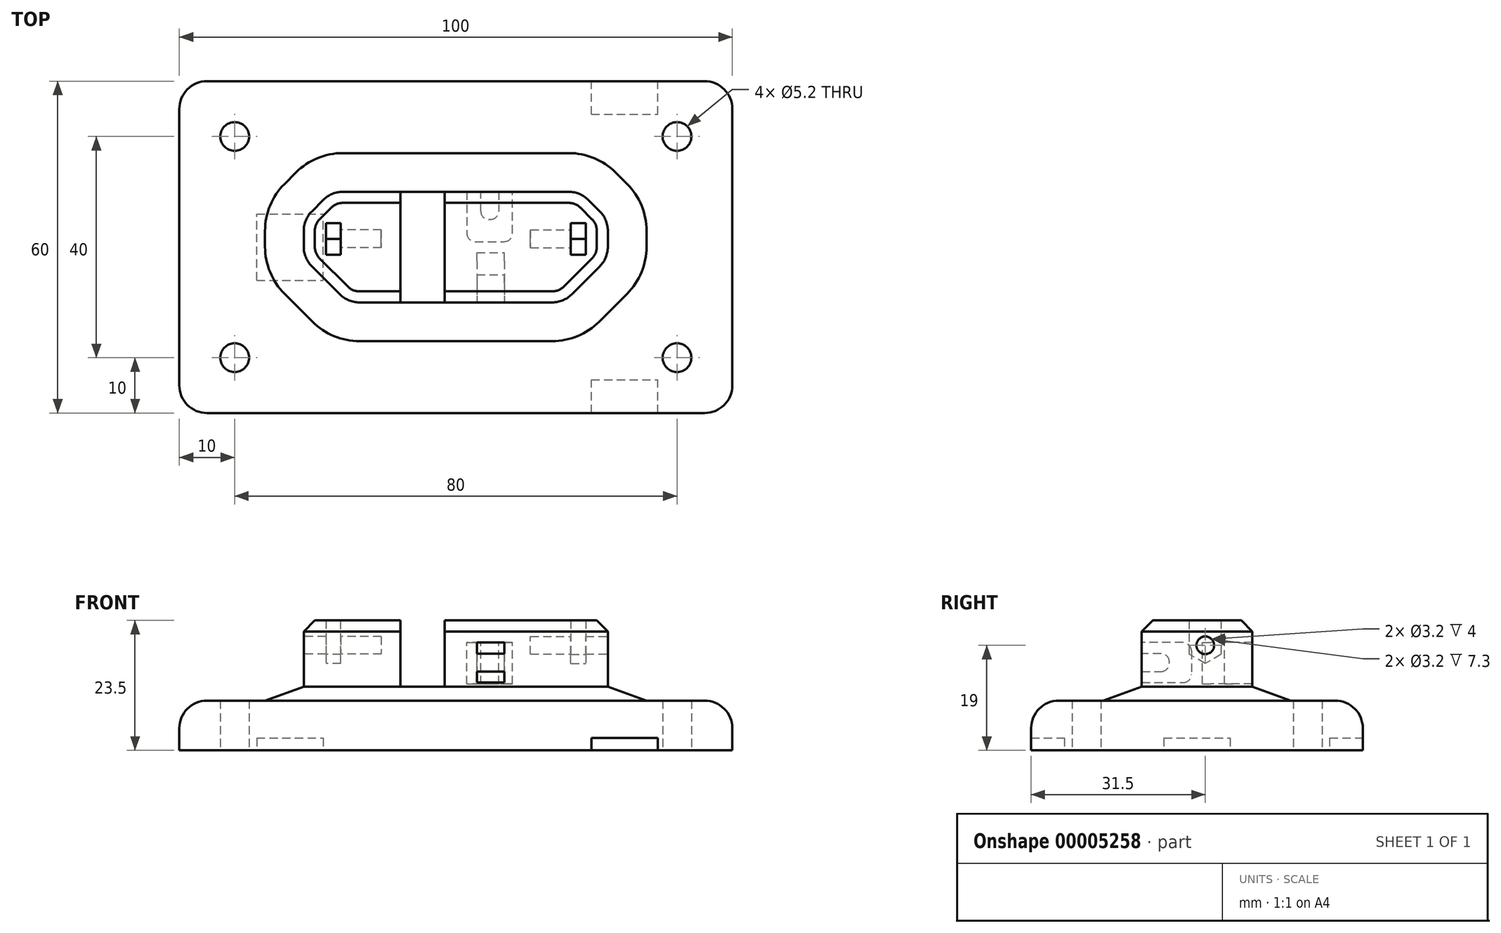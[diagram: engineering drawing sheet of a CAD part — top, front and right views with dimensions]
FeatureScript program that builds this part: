
annotation { "Feature Type Name" : "Feature", "Feature Type Description" : "" }
export const myFeature = defineFeature(function(context is Context, id is Id, definition is map)
    precondition{}
    {
        {
            var Q0;
            Q0=qCreatedBy(makeId("Top.planeOp"),FACE);
            var sketch = newSketch(context, id + "F0", { "sketchPlane" : qUnion([Q0])});
            skLineSegment(sketch, "E0.rect.bottom", {"start": v(-45, 30) * mm, "end": v(45, 30) * mm});
            skLineSegment(sketch, "E0.rect.top", {"start": v(-45, -30) * mm, "end": v(45, -30) * mm});
            skLineSegment(sketch, "E0.rect.left", {"start": v(-50, 25) * mm, "end": v(-50, -25) * mm});
            skLineSegment(sketch, "E0.rect.right", {"start": v(50, 25) * mm, "end": v(50, -25) * mm});
            skPoint(sketch, "E0.rect.middle", {"position": v(0, 0) * mm});
            skCircle(sketch, "E1", {"center": v(-40, 20) * mm, "radius": 2.6 * mm});
            skCircle(sketch, "E2", {"center": v(40, 20) * mm, "radius": 2.6 * mm});
            skCircle(sketch, "E3", {"center": v(40, -20) * mm, "radius": 2.6 * mm});
            skCircle(sketch, "E4", {"center": v(-40, -20) * mm, "radius": 2.6 * mm});
            skPoint(sketch, "E5.visualSharp", {"position": v(-50, 30) * mm});
            skArc(sketch, "E5.filletArc", {"start": v(-45, 30) * mm, "mid": v(-48.54, 28.54) * mm, "end": v(-50, 25) * mm});
            skPoint(sketch, "E6.visualSharp", {"position": v(50, 30) * mm});
            skArc(sketch, "E6.filletArc", {"start": v(50, 25) * mm, "mid": v(48.54, 28.54) * mm, "end": v(45, 30) * mm});
            skPoint(sketch, "E7.visualSharp", {"position": v(50, -30) * mm});
            skArc(sketch, "E7.filletArc", {"start": v(45, -30) * mm, "mid": v(48.54, -28.54) * mm, "end": v(50, -25) * mm});
            skPoint(sketch, "E8.visualSharp", {"position": v(-50, -30) * mm});
            skArc(sketch, "E8.filletArc", {"start": v(-50, -25) * mm, "mid": v(-48.54, -28.54) * mm, "end": v(-45, -30) * mm});
            skSolve(sketch);
        }
        {
            var Q0;
            Q0=qSketchRegion(id+"F0",true);
            extrude(context, id + "F1", {"entities" : qUnion([Q0]), "depth" : 9 * mm});
        }
        {
            var Q0;
            Q0=makeQuery(id+"F1.opExtrude","CAP_FACE",FACE,{"disambiguationData":[OSD([sQuery(id+"F0.wireOp",EDGE,"E0.rect.bottom"),sQuery(id+"F0.wireOp",EDGE,"E0.rect.top"),sQuery(id+"F0.wireOp",EDGE,"E0.rect.left"),sQuery(id+"F0.wireOp",EDGE,"E0.rect.right"),sQuery(id+"F0.wireOp",EDGE,"E1"),sQuery(id+"F0.wireOp",EDGE,"E2"),sQuery(id+"F0.wireOp",EDGE,"E3"),sQuery(id+"F0.wireOp",EDGE,"E4"),sQuery(id+"F0.wireOp",EDGE,"E5.filletArc"),sQuery(id+"F0.wireOp",EDGE,"E6.filletArc"),sQuery(id+"F0.wireOp",EDGE,"E7.filletArc"),sQuery(id+"F0.wireOp",EDGE,"E8.filletArc")])],"isStart":true});
            var sketch = newSketch(context, id + "F2", { "sketchPlane" : qUnion([Q0])});
            skLineSegment(sketch, "E9.rect.bottom", {"start": v(-36, 6) * mm, "end": v(-24, 6) * mm});
            skLineSegment(sketch, "E9.rect.top", {"start": v(-36, -6) * mm, "end": v(-24, -6) * mm});
            skLineSegment(sketch, "E9.rect.left", {"start": v(-36, 6) * mm, "end": v(-36, -6) * mm});
            skLineSegment(sketch, "E9.rect.right", {"start": v(-24, 6) * mm, "end": v(-24, -6) * mm});
            skPoint(sketch, "E9.rect.middle", {"position": v(-30, 0) * mm});
            skLineSegment(sketch, "E10.rect.bottom", {"start": v(24.52, 36) * mm, "end": v(36.52, 36) * mm});
            skLineSegment(sketch, "E10.rect.top", {"start": v(24.52, 24) * mm, "end": v(36.52, 24) * mm});
            skLineSegment(sketch, "E10.rect.left", {"start": v(24.52, 36) * mm, "end": v(24.52, 24) * mm});
            skLineSegment(sketch, "E10.rect.right", {"start": v(36.52, 36) * mm, "end": v(36.52, 24) * mm});
            skPoint(sketch, "E10.rect.middle", {"position": v(30.52, 30) * mm});
            skLineSegment(sketch, "E11.rect.bottom", {"start": v(24.52, -24) * mm, "end": v(36.52, -24) * mm});
            skLineSegment(sketch, "E11.rect.top", {"start": v(24.52, -36) * mm, "end": v(36.52, -36) * mm});
            skLineSegment(sketch, "E11.rect.left", {"start": v(24.52, -24) * mm, "end": v(24.52, -36) * mm});
            skLineSegment(sketch, "E11.rect.right", {"start": v(36.52, -24) * mm, "end": v(36.52, -36) * mm});
            skPoint(sketch, "E11.rect.middle", {"position": v(30.52, -30) * mm});
            skLineSegment(sketch, "E12", {"start": v(0, 0) * mm, "end": v(50, 0) * mm});
            skSolve(sketch);
        }
        {
            var Q0;
            Q0=qSketchRegion(id+"F2",true);
            extrude(context, id + "F3", {"entities" : qUnion([Q0]), "operationType" : NewBodyOperationType.REMOVE, "oppositeDirection" : true, "depth" : 2.25 * mm});
        }
        {
            var Q0;
            Q0=makeQuery(id+"F1.opExtrude","CAP_FACE",FACE,{"disambiguationData":[OSD([sQuery(id+"F0.wireOp",EDGE,"E0.rect.bottom"),sQuery(id+"F0.wireOp",EDGE,"E0.rect.top"),sQuery(id+"F0.wireOp",EDGE,"E0.rect.left"),sQuery(id+"F0.wireOp",EDGE,"E0.rect.right"),sQuery(id+"F0.wireOp",EDGE,"E1"),sQuery(id+"F0.wireOp",EDGE,"E2"),sQuery(id+"F0.wireOp",EDGE,"E3"),sQuery(id+"F0.wireOp",EDGE,"E4"),sQuery(id+"F0.wireOp",EDGE,"E5.filletArc"),sQuery(id+"F0.wireOp",EDGE,"E6.filletArc"),sQuery(id+"F0.wireOp",EDGE,"E7.filletArc"),sQuery(id+"F0.wireOp",EDGE,"E8.filletArc")])],"isStart":false});
            var sketch = newSketch(context, id + "F4", { "sketchPlane" : qUnion([Q0])});
            skPoint(sketch, "E13.orphan", {"position": v(-50, 0) * mm});
            skPoint(sketch, "E14.end.orphan", {"position": v(50, 0) * mm});
            skLineSegment(sketch, "E15.rect.bottom", {"start": v(-27.5, 10) * mm, "end": v(27.5, 10) * mm});
            skLineSegment(sketch, "E15.rect.top", {"start": v(-27.5, -10) * mm, "end": v(27.5, -10) * mm});
            skLineSegment(sketch, "E15.rect.left", {"start": v(-27.5, 10) * mm, "end": v(-27.5, -10) * mm});
            skLineSegment(sketch, "E15.rect.right", {"start": v(27.5, 10) * mm, "end": v(27.5, -10) * mm});
            skPoint(sketch, "E15.rect.middle", {"position": v(0, 0) * mm});
            skSolve(sketch);
        }
        {
            var Q0;
            Q0=qSketchRegion(id+"F4",true);
            extrude(context, id + "F5", {"entities" : qUnion([Q0]), "operationType" : NewBodyOperationType.ADD, "depth" : 14.5 * mm});
        }
        {
            var Q0;
            Q0=makeQuery(id+"F5.opExtrude","SWEPT_EDGE",EDGE,{"disambiguationData":[OSD([sQuery(id+"F4.wireOp",EDGE,"E15.rect.top"),sQuery(id+"F4.wireOp",EDGE,"E15.rect.left")])]});
            var Q1;
            Q1=makeQuery(id+"F5.opExtrude","SWEPT_EDGE",EDGE,{"disambiguationData":[OSD([sQuery(id+"F4.wireOp",EDGE,"E15.rect.top"),sQuery(id+"F4.wireOp",EDGE,"E15.rect.right")])]});
            chamfer(context, id + "F6", {"entities" : qUnion([Q0, Q1]), "width" : 8 * mm, "tangentPropagation" : true});
        }
        {
            var Q0;
            Q0=makeQuery(id+"F5.opExtrude","SWEPT_EDGE",EDGE,{"disambiguationData":[OSD([sQuery(id+"F4.wireOp",EDGE,"E15.rect.bottom"),sQuery(id+"F4.wireOp",EDGE,"E15.rect.left")])]});
            var Q1;
            Q1=makeQuery(id+"F5.opExtrude","SWEPT_EDGE",EDGE,{"disambiguationData":[OSD([sQuery(id+"F4.wireOp",EDGE,"E15.rect.bottom"),sQuery(id+"F4.wireOp",EDGE,"E15.rect.right")])]});
            chamfer(context, id + "F7", {"entities" : qUnion([Q0, Q1]), "width" : 5 * mm, "tangentPropagation" : true});
        }
        {
            var Q0;
            Q0=makeQuery(id+"F5.opExtrude","CAP_FACE",FACE,{"disambiguationData":[OSD([sQuery(id+"F4.wireOp",EDGE,"E15.rect.bottom"),sQuery(id+"F4.wireOp",EDGE,"E15.rect.top"),sQuery(id+"F4.wireOp",EDGE,"E15.rect.left"),sQuery(id+"F4.wireOp",EDGE,"E15.rect.right")])],"isStart":false});
            var sketch = newSketch(context, id + "F8", { "sketchPlane" : qUnion([Q0])});
            skLineSegment(sketch, "E16.rect.bottom", {"start": v(-10, 10) * mm, "end": v(-2, 10) * mm});
            skLineSegment(sketch, "E16.rect.top", {"start": v(-10, -10) * mm, "end": v(-2, -10) * mm});
            skLineSegment(sketch, "E16.rect.left", {"start": v(-10, 10) * mm, "end": v(-10, -10) * mm});
            skLineSegment(sketch, "E16.rect.right", {"start": v(-2, 10) * mm, "end": v(-2, -10) * mm});
            skPoint(sketch, "E16.rect.middle", {"position": v(-6, 0) * mm});
            skSolve(sketch);
        }
        {
            var Q0;
            Q0=qSketchRegion(id+"F8",true);
            extrude(context, id + "F9", {"entities" : qUnion([Q0]), "operationType" : NewBodyOperationType.REMOVE, "oppositeDirection" : true, "depth" : 12 * mm});
        }
        {
            var Q0;
            {var subQ0=sQuery(id+"F4.wireOp",EDGE,"E15.rect.bottom");var subQ1=sQuery(id+"F4.wireOp",EDGE,"E15.rect.top");var subQ2=sQuery(id+"F4.wireOp",EDGE,"E15.rect.right");Q0=makeQuery(id+"F9.boolean.opBoolean","SPLIT",FACE,{"disambiguationData":[TD([makeQuery(id+"F5.opExtrude","SWEPT_FACE",FACE,{"disambiguationData":[OSD([subQ2])]})])],"derivedFrom":makeQuery(id+"F5.opExtrude","CAP_FACE",FACE,{"disambiguationData":[OSD([subQ0,subQ1,sQuery(id+"F4.wireOp",EDGE,"E15.rect.left"),subQ2])],"isStart":false})});}
            cPlane(context, id + "F10", {"entities" : qUnion([Q0]), "cplaneType" : CPlaneType.OFFSET, "offset" : 4 * mm, "oppositeDirection" : true, "width" : 150 * mm, "height" : 150 * mm});
        }
        {
            var Q0;
            Q0=makeQuery(id+"F5.opExtrude","SWEPT_FACE",FACE,{"disambiguationData":[OSD([sQuery(id+"F4.wireOp",EDGE,"E15.rect.left")])]});
            var sketch = newSketch(context, id + "F11", { "sketchPlane" : qUnion([Q0])});
            skCircle(sketch, "E17", {"center": v(-1.5, 19) * mm, "radius": 1.6 * mm});
            skSolve(sketch);
        }
        {
            var Q0;
            Q0=qSketchRegion(id+"F11",true);
            extrude(context, id + "F12", {"entities" : qUnion([Q0]), "operationType" : NewBodyOperationType.REMOVE, "oppositeDirection" : true, "depth" : 14 * mm});
        }
        {
            var Q0;
            Q0=makeQuery(id+"F5.opExtrude","SWEPT_FACE",FACE,{"disambiguationData":[OSD([sQuery(id+"F4.wireOp",EDGE,"E15.rect.right")])]});
            var sketch = newSketch(context, id + "F13", { "sketchPlane" : qUnion([Q0])});
            skCircle(sketch, "E18", {"center": v(1.5, 19) * mm, "radius": 1.6 * mm});
            skSolve(sketch);
        }
        {
            var Q0;
            Q0=qSketchRegion(id+"F13",true);
            extrude(context, id + "F14", {"entities" : qUnion([Q0]), "operationType" : NewBodyOperationType.REMOVE, "oppositeDirection" : true, "depth" : 14 * mm});
        }
        {
            var Q0;
            Q0=qCreatedBy(id+"F10.planeOp",FACE);
            var sketch = newSketch(context, id + "F15", { "sketchPlane" : qUnion([Q0])});
            skLineSegment(sketch, "E19", {"start": v(2, 10) * mm, "end": v(2, 1) * mm});
            skLineSegment(sketch, "E20", {"start": v(2, 1) * mm, "end": v(10.25, 1) * mm});
            skLineSegment(sketch, "E21", {"start": v(10.25, 1) * mm, "end": v(10.25, 10) * mm});
            skLineSegment(sketch, "E22", {"start": v(10.25, 10) * mm, "end": v(7.75, 10) * mm});
            skLineSegment(sketch, "E23", {"start": v(7.75, 10) * mm, "end": v(7.75, 5) * mm});
            skLineSegment(sketch, "E24", {"start": v(7.75, 5) * mm, "end": v(4.5, 5) * mm});
            skLineSegment(sketch, "E25", {"start": v(4.5, 5) * mm, "end": v(4.5, 10) * mm});
            skLineSegment(sketch, "E26", {"start": v(4.5, 10) * mm, "end": v(2, 10) * mm});
            skSolve(sketch);
        }
        {
            var Q0;
            Q0=qSketchRegion(id+"F15",true);
            extrude(context, id + "F16", {"entities" : qUnion([Q0]), "operationType" : NewBodyOperationType.REMOVE, "oppositeDirection" : true, "depth" : 7.5 * mm});
        }
        {
            var Q0;
            Q0=qCreatedBy(makeId("Right.planeOp"),FACE);
            cPlane(context, id + "F17", {"entities" : qUnion([Q0]), "cplaneType" : CPlaneType.OFFSET, "offset" : 8.8 * mm, "width" : 150 * mm, "height" : 150 * mm});
        }
        {
            var Q0;
            Q0=qCreatedBy(id+"F17.planeOp",FACE);
            var sketch = newSketch(context, id + "F18", { "sketchPlane" : qUnion([Q0])});
            skLineSegment(sketch, "E27", {"start": v(-10, 12.25) * mm, "end": v(-1, 12.25) * mm});
            skLineSegment(sketch, "E28", {"start": v(-1, 19.5) * mm, "end": v(-10, 19.5) * mm});
            skLineSegment(sketch, "E29", {"start": v(-10, 19.5) * mm, "end": v(-10, 17.5) * mm});
            skLineSegment(sketch, "E30", {"start": v(-1, 19.5) * mm, "end": v(-1, 12.25) * mm});
            skLineSegment(sketch, "E31", {"start": v(-10, 14.25) * mm, "end": v(-5, 14.25) * mm});
            skLineSegment(sketch, "E32", {"start": v(-5, 14.25) * mm, "end": v(-5, 17.5) * mm});
            skLineSegment(sketch, "E33", {"start": v(-5, 17.5) * mm, "end": v(-10, 17.5) * mm});
            skLineSegment(sketch, "E34.trimOffspring", {"start": v(-10, 14.25) * mm, "end": v(-10, 12.25) * mm});
            skSolve(sketch);
        }
        {
            var Q0;
            Q0 = qSketchRegion(id + "F18", true);
            extrude(context, id + "F19", {"entities" : qUnion([Q0]), "operationType" : NewBodyOperationType.REMOVE, "oppositeDirection" : true, "depth" : 5 * mm});
        }
        {
            var Q0;
            Q0=makeQuery(id+"F16.boolean.opBoolean","COPY",EDGE,{"derivedFrom":makeQuery(id+"F16.opExtrude","SWEPT_EDGE",EDGE,{"disambiguationData":[OSD([sQuery(id+"F15.wireOp",EDGE,"b27fa09f-654b-4976-832a-8cd4d72e1bcd"),sQuery(id+"F15.wireOp",EDGE,"0d0e19da-8f42-4381-b15f-3c7ce20022dd")])]})});
            var Q1;
            Q1=makeQuery(id+"F16.boolean.opBoolean","COPY",EDGE,{"derivedFrom":makeQuery(id+"F16.opExtrude","SWEPT_EDGE",EDGE,{"disambiguationData":[OSD([sQuery(id+"F15.wireOp",EDGE,"0d0e19da-8f42-4381-b15f-3c7ce20022dd"),sQuery(id+"F15.wireOp",EDGE,"007b9c6f-361a-4d94-a8b3-a32368527ee9")])]})});
            var Q2;
            Q2=makeQuery(id+"F16.boolean.opBoolean","COPY",EDGE,{"derivedFrom":makeQuery(id+"F16.opExtrude","SWEPT_EDGE",EDGE,{"disambiguationData":[OSD([sQuery(id+"F15.wireOp",EDGE,"966db383-c47d-4d1a-9eee-fc0741a5b44d"),sQuery(id+"F15.wireOp",EDGE,"9a90bedf-13ad-46d5-b3b2-74371d44ae28")])]})});
            var Q3;
            Q3=makeQuery(id+"F16.boolean.opBoolean","COPY",EDGE,{"derivedFrom":makeQuery(id+"F16.opExtrude","SWEPT_EDGE",EDGE,{"disambiguationData":[OSD([sQuery(id+"F15.wireOp",EDGE,"9a90bedf-13ad-46d5-b3b2-74371d44ae28"),sQuery(id+"F15.wireOp",EDGE,"3751e907-f0bc-4d0a-a093-d6da3d786c70")])]})});
            var Q4;
            Q4=makeQuery(id+"F16.boolean.opBoolean","COPY",EDGE,{"derivedFrom":makeQuery(id+"F16.opExtrude","SWEPT_EDGE",EDGE,{"disambiguationData":[OSD([sQuery(id+"F15.wireOp",EDGE,"E24"),sQuery(id+"F15.wireOp",EDGE,"E25")])]})});
            var Q5;
            Q5=makeQuery(id+"F16.boolean.opBoolean","COPY",EDGE,{"derivedFrom":makeQuery(id+"F16.opExtrude","SWEPT_EDGE",EDGE,{"disambiguationData":[OSD([sQuery(id+"F15.wireOp",EDGE,"E23"),sQuery(id+"F15.wireOp",EDGE,"E24")])]})});
            var Q6;
            Q6=makeQuery(id+"F16.boolean.opBoolean","COPY",EDGE,{"derivedFrom":makeQuery(id+"F16.opExtrude","SWEPT_EDGE",EDGE,{"disambiguationData":[OSD([sQuery(id+"F15.wireOp",EDGE,"E19"),sQuery(id+"F15.wireOp",EDGE,"E20")])]})});
            var Q7;
            Q7=makeQuery(id+"F16.boolean.opBoolean","COPY",EDGE,{"derivedFrom":makeQuery(id+"F16.opExtrude","SWEPT_EDGE",EDGE,{"disambiguationData":[OSD([sQuery(id+"F15.wireOp",EDGE,"E20"),sQuery(id+"F15.wireOp",EDGE,"E21")])]})});
            var Q8;
            Q8=makeQuery(id+"F19.boolean.opBoolean","COPY",EDGE,{"derivedFrom":makeQuery(id+"F19.opExtrude","SWEPT_EDGE",EDGE,{"disambiguationData":[OSD([sQuery(id+"F18.wireOp",EDGE,"E32"),sQuery(id+"F18.wireOp",EDGE,"E33")])]})});
            var Q9;
            Q9=makeQuery(id+"F19.boolean.opBoolean","COPY",EDGE,{"derivedFrom":makeQuery(id+"F19.opExtrude","SWEPT_EDGE",EDGE,{"disambiguationData":[OSD([sQuery(id+"F18.wireOp",EDGE,"E31"),sQuery(id+"F18.wireOp",EDGE,"E32")])]})});
            var Q10;
            Q10=makeQuery(id+"F19.boolean.opBoolean","COPY",EDGE,{"derivedFrom":makeQuery(id+"F19.opExtrude","SWEPT_EDGE",EDGE,{"disambiguationData":[OSD([sQuery(id+"F18.wireOp",EDGE,"E28"),sQuery(id+"F18.wireOp",EDGE,"E30")])]})});
            var Q11;
            Q11=makeQuery(id+"F19.boolean.opBoolean","COPY",EDGE,{"derivedFrom":makeQuery(id+"F19.opExtrude","SWEPT_EDGE",EDGE,{"disambiguationData":[OSD([sQuery(id+"F18.wireOp",EDGE,"E27"),sQuery(id+"F18.wireOp",EDGE,"E30")])]})});
            fillet(context, id + "F20", {"entities" : qUnion([Q0, Q1, Q2, Q3, Q4, Q5, Q6, Q7, Q8, Q9, Q10, Q11]), "radius" : 1.5 * mm, "tangentPropagation" : true, "allowEdgeOverflow" : false});
        }
        {
            var Q0;
            Q0=makeQuery(id+"F5.opExtrude","SWEPT_FACE",FACE,{"disambiguationData":[OSD([sQuery(id+"F4.wireOp",EDGE,"E15.rect.right")])]});
            cPlane(context, id + "F21", {"entities" : qUnion([Q0]), "cplaneType" : CPlaneType.OFFSET, "offset" : 4 * mm, "oppositeDirection" : true, "width" : 150 * mm, "height" : 150 * mm});
        }
        {
            var Q0;
            Q0=qCreatedBy(id+"F21.planeOp",FACE);
            var sketch = newSketch(context, id + "F22", { "sketchPlane" : qUnion([Q0])});
            skCircle(sketch, "E35.cCircle", {"center": v(1.5, 19) * mm, "radius": 2.85 * mm, "construction": true});
            skLineSegment(sketch, "E35.0", {"start": v(-1.35, 17.35) * mm, "end": v(-1.35, 20.65) * mm});
            skLineSegment(sketch, "E35.1", {"start": v(-1.35, 20.65) * mm, "end": v(1.5, 22.3) * mm});
            skLineSegment(sketch, "E35.2", {"start": v(1.5, 22.3) * mm, "end": v(4.35, 20.65) * mm});
            skLineSegment(sketch, "E35.3", {"start": v(4.35, 20.65) * mm, "end": v(4.35, 17.35) * mm});
            skLineSegment(sketch, "E35.4", {"start": v(4.35, 17.35) * mm, "end": v(1.5, 15.7) * mm});
            skLineSegment(sketch, "E35.5", {"start": v(1.5, 15.7) * mm, "end": v(-1.35, 17.35) * mm});
            skPoint(sketch, "E35.0.midPoint", {"position": v(-1.35, 19) * mm});
            skLineSegment(sketch, "E36", {"start": v(-1.35, 20.65) * mm, "end": v(-1.35, 23.5) * mm});
            skLineSegment(sketch, "E37", {"start": v(-1.35, 23.5) * mm, "end": v(4.35, 23.5) * mm});
            skLineSegment(sketch, "E38", {"start": v(4.35, 23.5) * mm, "end": v(4.35, 20.65) * mm});
            skSolve(sketch);
        }
        {
            var Q0;
            Q0=qSketchRegion(id+"F22",true);
            extrude(context, id + "F23", {"entities" : qUnion([Q0]), "operationType" : NewBodyOperationType.REMOVE, "oppositeDirection" : true, "depth" : 2.7 * mm});
        }
        {
            var Q0;
            Q0=makeQuery(id+"F5.opExtrude","SWEPT_FACE",FACE,{"disambiguationData":[OSD([sQuery(id+"F4.wireOp",EDGE,"E15.rect.left")])]});
            cPlane(context, id + "F24", {"entities" : qUnion([Q0]), "cplaneType" : CPlaneType.OFFSET, "offset" : 4 * mm, "oppositeDirection" : true, "width" : 150 * mm, "height" : 150 * mm});
        }
        {
            var Q0;
            Q0=qCreatedBy(id+"F24.planeOp",FACE);
            var sketch = newSketch(context, id + "F25", { "sketchPlane" : qUnion([Q0])});
            skCircle(sketch, "E39.cCircle", {"center": v(-1.5, 19) * mm, "radius": 2.85 * mm, "construction": true});
            skLineSegment(sketch, "E39.0", {"start": v(-4.35, 20.65) * mm, "end": v(-1.5, 22.3) * mm});
            skLineSegment(sketch, "E39.1", {"start": v(-1.5, 22.3) * mm, "end": v(1.35, 20.65) * mm});
            skLineSegment(sketch, "E39.2", {"start": v(1.35, 20.65) * mm, "end": v(1.35, 17.35) * mm});
            skLineSegment(sketch, "E39.3", {"start": v(1.35, 17.35) * mm, "end": v(-1.5, 15.7) * mm});
            skLineSegment(sketch, "E39.4", {"start": v(-1.5, 15.7) * mm, "end": v(-4.35, 17.35) * mm});
            skLineSegment(sketch, "E39.5", {"start": v(-4.35, 17.35) * mm, "end": v(-4.35, 20.65) * mm});
            skPoint(sketch, "E39.0.midPoint", {"position": v(-2.92, 21.47) * mm});
            skLineSegment(sketch, "E40", {"start": v(-4.35, 20.65) * mm, "end": v(-4.35, 23.5) * mm});
            skLineSegment(sketch, "E41", {"start": v(-4.35, 23.5) * mm, "end": v(1.35, 23.5) * mm});
            skLineSegment(sketch, "E42", {"start": v(1.35, 23.5) * mm, "end": v(1.35, 20.65) * mm});
            skSolve(sketch);
        }
        {
            var Q0;
            Q0=qSketchRegion(id+"F25",true);
            extrude(context, id + "F26", {"entities" : qUnion([Q0]), "operationType" : NewBodyOperationType.REMOVE, "oppositeDirection" : true, "depth" : 2.7 * mm});
        }
        {
            var Q0;
            Q0=makeQuery(id+"F1.opExtrude","CAP_EDGE",EDGE,{"disambiguationData":[OSD([sQuery(id+"F0.wireOp",EDGE,"E0.rect.top")])],"isStart":false});
            fillet(context, id + "F27", {"entities" : qUnion([Q0]), "radius" : 5 * mm, "tangentPropagation" : true, "allowEdgeOverflow" : false});
        }
        {
            var Q0;
            {var subQ0=sQuery(id+"F4.wireOp",EDGE,"E15.rect.top");Q0=makeQuery(id+"F6.opChamfer","BLEND_EDGE",EDGE,{"blendedFrom":[makeQuery(id+"F5.opExtrude","SWEPT_EDGE",EDGE,{"disambiguationData":[OSD([subQ0,sQuery(id+"F4.wireOp",EDGE,"E15.rect.left")])]}),makeQuery(id+"F5.opExtrude","SWEPT_FACE",FACE,{"disambiguationData":[OSD([subQ0])]})],"blendedInto":[makeQuery(id+"F5.opExtrude","SWEPT_FACE",FACE,{"disambiguationData":[OSD([subQ0])]})]});}
            var Q1;
            {var subQ0=sQuery(id+"F4.wireOp",EDGE,"E15.rect.left");Q1=makeQuery(id+"F6.opChamfer","BLEND_EDGE",EDGE,{"blendedFrom":[makeQuery(id+"F5.opExtrude","SWEPT_EDGE",EDGE,{"disambiguationData":[OSD([sQuery(id+"F4.wireOp",EDGE,"E15.rect.top"),subQ0])]}),makeQuery(id+"F5.opExtrude","SWEPT_FACE",FACE,{"disambiguationData":[OSD([subQ0])]})],"blendedInto":[makeQuery(id+"F5.opExtrude","SWEPT_FACE",FACE,{"disambiguationData":[OSD([subQ0])]})]});}
            var Q2;
            {var subQ0=sQuery(id+"F4.wireOp",EDGE,"E15.rect.left");Q2=makeQuery(id+"F7.opChamfer","BLEND_EDGE",EDGE,{"blendedFrom":[makeQuery(id+"F5.opExtrude","SWEPT_EDGE",EDGE,{"disambiguationData":[OSD([sQuery(id+"F4.wireOp",EDGE,"E15.rect.bottom"),subQ0])]}),makeQuery(id+"F5.opExtrude","SWEPT_FACE",FACE,{"disambiguationData":[OSD([subQ0])]})],"blendedInto":[makeQuery(id+"F5.opExtrude","SWEPT_FACE",FACE,{"disambiguationData":[OSD([subQ0])]})]});}
            var Q3;
            {var subQ0=sQuery(id+"F4.wireOp",EDGE,"E15.rect.bottom");Q3=makeQuery(id+"F7.opChamfer","BLEND_EDGE",EDGE,{"blendedFrom":[makeQuery(id+"F5.opExtrude","SWEPT_EDGE",EDGE,{"disambiguationData":[OSD([subQ0,sQuery(id+"F4.wireOp",EDGE,"E15.rect.left")])]}),makeQuery(id+"F5.opExtrude","SWEPT_FACE",FACE,{"disambiguationData":[OSD([subQ0])]})],"blendedInto":[makeQuery(id+"F5.opExtrude","SWEPT_FACE",FACE,{"disambiguationData":[OSD([subQ0])]})]});}
            var Q4;
            Q4=makeQuery(id+"F9.boolean.opBoolean","COPY",EDGE,{"derivedFrom":makeQuery(id+"F9.opExtrude","SWEPT_EDGE",EDGE,{"disambiguationData":[OSD([sQuery(id+"F4.wireOp",EDGE,"E15.rect.top"),sQuery(id+"F8.wireOp",EDGE,"E16.rect.top"),sQuery(id+"F8.wireOp",EDGE,"E16.rect.left")])]})});
            var Q5;
            Q5=makeQuery(id+"F9.boolean.opBoolean","COPY",EDGE,{"derivedFrom":makeQuery(id+"F9.opExtrude","SWEPT_EDGE",EDGE,{"disambiguationData":[OSD([sQuery(id+"F4.wireOp",EDGE,"E15.rect.bottom"),sQuery(id+"F8.wireOp",EDGE,"E16.rect.bottom"),sQuery(id+"F8.wireOp",EDGE,"E16.rect.left")])]})});
            var Q6;
            Q6=makeQuery(id+"F9.boolean.opBoolean","COPY",EDGE,{"derivedFrom":makeQuery(id+"F9.opExtrude","SWEPT_EDGE",EDGE,{"disambiguationData":[OSD([sQuery(id+"F4.wireOp",EDGE,"E15.rect.bottom"),sQuery(id+"F8.wireOp",EDGE,"E16.rect.bottom"),sQuery(id+"F8.wireOp",EDGE,"E16.rect.right")])]})});
            var Q7;
            Q7=makeQuery(id+"F9.boolean.opBoolean","COPY",EDGE,{"derivedFrom":makeQuery(id+"F9.opExtrude","SWEPT_EDGE",EDGE,{"disambiguationData":[OSD([sQuery(id+"F4.wireOp",EDGE,"E15.rect.top"),sQuery(id+"F8.wireOp",EDGE,"E16.rect.top"),sQuery(id+"F8.wireOp",EDGE,"E16.rect.right")])]})});
            var Q8;
            {var subQ0=sQuery(id+"F4.wireOp",EDGE,"E15.rect.top");Q8=makeQuery(id+"F6.opChamfer","BLEND_EDGE",EDGE,{"blendedFrom":[makeQuery(id+"F5.opExtrude","SWEPT_EDGE",EDGE,{"disambiguationData":[OSD([subQ0,sQuery(id+"F4.wireOp",EDGE,"E15.rect.right")])]}),makeQuery(id+"F5.opExtrude","SWEPT_FACE",FACE,{"disambiguationData":[OSD([subQ0])]})],"blendedInto":[makeQuery(id+"F5.opExtrude","SWEPT_FACE",FACE,{"disambiguationData":[OSD([subQ0])]})]});}
            var Q9;
            {var subQ0=sQuery(id+"F4.wireOp",EDGE,"E15.rect.right");Q9=makeQuery(id+"F6.opChamfer","BLEND_EDGE",EDGE,{"blendedFrom":[makeQuery(id+"F5.opExtrude","SWEPT_EDGE",EDGE,{"disambiguationData":[OSD([sQuery(id+"F4.wireOp",EDGE,"E15.rect.top"),subQ0])]}),makeQuery(id+"F5.opExtrude","SWEPT_FACE",FACE,{"disambiguationData":[OSD([subQ0])]})],"blendedInto":[makeQuery(id+"F5.opExtrude","SWEPT_FACE",FACE,{"disambiguationData":[OSD([subQ0])]})]});}
            var Q10;
            {var subQ0=sQuery(id+"F4.wireOp",EDGE,"E15.rect.right");Q10=makeQuery(id+"F7.opChamfer","BLEND_EDGE",EDGE,{"blendedFrom":[makeQuery(id+"F5.opExtrude","SWEPT_EDGE",EDGE,{"disambiguationData":[OSD([sQuery(id+"F4.wireOp",EDGE,"E15.rect.bottom"),subQ0])]}),makeQuery(id+"F5.opExtrude","SWEPT_FACE",FACE,{"disambiguationData":[OSD([subQ0])]})],"blendedInto":[makeQuery(id+"F5.opExtrude","SWEPT_FACE",FACE,{"disambiguationData":[OSD([subQ0])]})]});}
            var Q11;
            {var subQ0=sQuery(id+"F4.wireOp",EDGE,"E15.rect.bottom");Q11=makeQuery(id+"F7.opChamfer","BLEND_EDGE",EDGE,{"blendedFrom":[makeQuery(id+"F5.opExtrude","SWEPT_EDGE",EDGE,{"disambiguationData":[OSD([subQ0,sQuery(id+"F4.wireOp",EDGE,"E15.rect.right")])]}),makeQuery(id+"F5.opExtrude","SWEPT_FACE",FACE,{"disambiguationData":[OSD([subQ0])]})],"blendedInto":[makeQuery(id+"F5.opExtrude","SWEPT_FACE",FACE,{"disambiguationData":[OSD([subQ0])]})]});}
            fillet(context, id + "F28", {"entities" : qUnion([Q0, Q1, Q2, Q3, Q4, Q5, Q6, Q7, Q8, Q9, Q10, Q11]), "radius" : 5 * mm, "tangentPropagation" : true, "allowEdgeOverflow" : false});
        }
        {
            var Q0;
            Q0=makeQuery(id+"F5.opExtrude","CAP_EDGE",EDGE,{"disambiguationData":[OSD([sQuery(id+"F4.wireOp",EDGE,"E15.rect.left")])],"isStart":false});
            var Q1;
            Q1=makeQuery(id+"F5.opExtrude","CAP_EDGE",EDGE,{"disambiguationData":[OSD([sQuery(id+"F4.wireOp",EDGE,"E15.rect.right")])],"isStart":false});
            chamfer(context, id + "F29", {"entities" : qUnion([Q0, Q1]), "width" : 2 * mm, "tangentPropagation" : true});
        }
        {
            var Q0;
            Q0=makeQuery(id+"F6.opChamfer","BLEND_EDGE",EDGE,{"blendedFrom":[makeQuery(id+"F5.opExtrude","SWEPT_EDGE",EDGE,{"disambiguationData":[OSD([sQuery(id+"F4.wireOp",EDGE,"E15.rect.top"),sQuery(id+"F4.wireOp",EDGE,"E15.rect.left")])]}),makeQuery(id+"F1.opExtrude","CAP_FACE",FACE,{"disambiguationData":[OSD([sQuery(id+"F0.wireOp",EDGE,"E0.rect.bottom"),sQuery(id+"F0.wireOp",EDGE,"E0.rect.top"),sQuery(id+"F0.wireOp",EDGE,"E0.rect.left"),sQuery(id+"F0.wireOp",EDGE,"E0.rect.right"),sQuery(id+"F0.wireOp",EDGE,"E1"),sQuery(id+"F0.wireOp",EDGE,"E2"),sQuery(id+"F0.wireOp",EDGE,"E3"),sQuery(id+"F0.wireOp",EDGE,"E4"),sQuery(id+"F0.wireOp",EDGE,"E5.filletArc"),sQuery(id+"F0.wireOp",EDGE,"E6.filletArc"),sQuery(id+"F0.wireOp",EDGE,"E7.filletArc"),sQuery(id+"F0.wireOp",EDGE,"E8.filletArc")])],"isStart":false})],"blendedInto":[makeQuery(id+"F1.opExtrude","CAP_FACE",FACE,{"disambiguationData":[OSD([sQuery(id+"F0.wireOp",EDGE,"E0.rect.bottom"),sQuery(id+"F0.wireOp",EDGE,"E0.rect.top"),sQuery(id+"F0.wireOp",EDGE,"E0.rect.left"),sQuery(id+"F0.wireOp",EDGE,"E0.rect.right"),sQuery(id+"F0.wireOp",EDGE,"E1"),sQuery(id+"F0.wireOp",EDGE,"E2"),sQuery(id+"F0.wireOp",EDGE,"E3"),sQuery(id+"F0.wireOp",EDGE,"E4"),sQuery(id+"F0.wireOp",EDGE,"E5.filletArc"),sQuery(id+"F0.wireOp",EDGE,"E6.filletArc"),sQuery(id+"F0.wireOp",EDGE,"E7.filletArc"),sQuery(id+"F0.wireOp",EDGE,"E8.filletArc")])],"isStart":false})]});
            chamfer(context, id + "F30", {"entities" : qUnion([Q0]), "chamferType" : ChamferType.TWO_OFFSETS, "width1" : 7 * mm, "oppositeDirection" : false, "width2" : 2.5 * mm, "tangentPropagation" : true});
        }
    });
